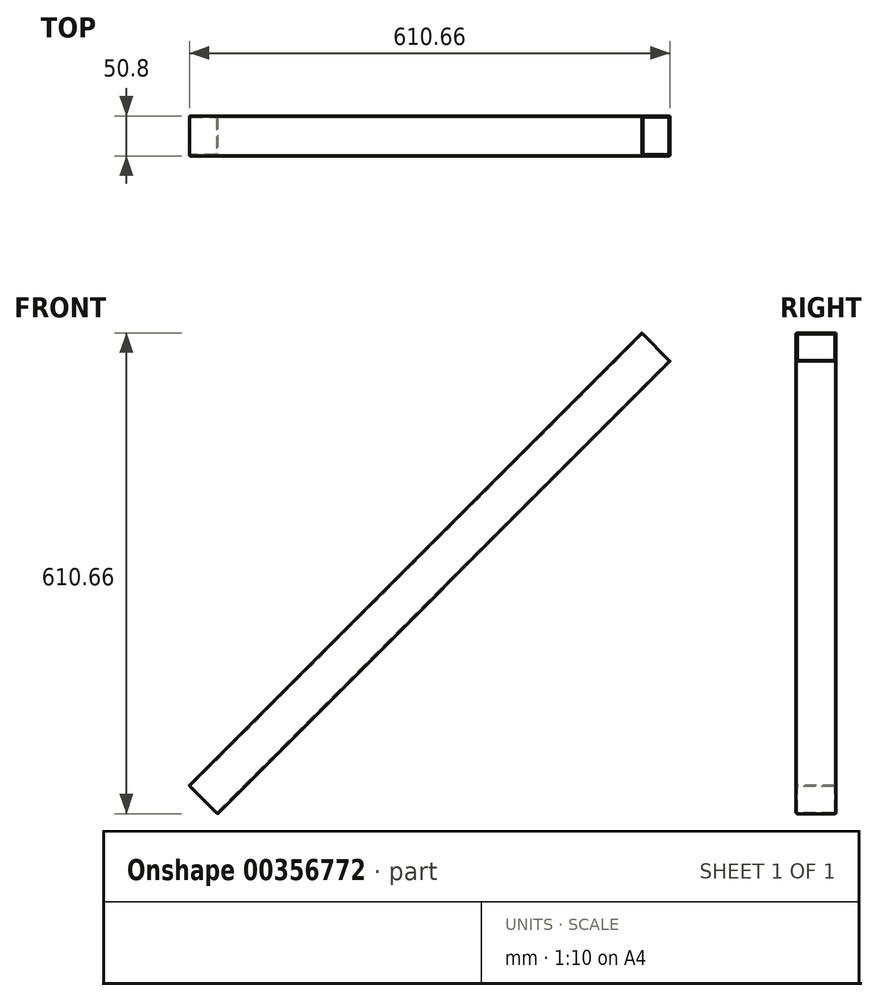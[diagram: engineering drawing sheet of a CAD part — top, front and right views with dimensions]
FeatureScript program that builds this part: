
annotation { "Feature Type Name" : "Feature", "Feature Type Description" : "" }
export const myFeature = defineFeature(function(context is Context, id is Id, definition is map)
    precondition{}
    {
        {
            var Q0;
            Q0=qCreatedBy(makeId("Front.planeOp"),FACE);
            var sketch = newSketch(context, id + "F0", { "sketchPlane" : qUnion([Q0])});
            skLineSegment(sketch, "E0.bottom", {"start": v(762, -381) * mm, "end": v(-762, -381) * mm});
            skLineSegment(sketch, "E0.top", {"start": v(762, 381) * mm, "end": v(-762, 381) * mm});
            skLineSegment(sketch, "E0.left", {"start": v(762, -381) * mm, "end": v(762, 381) * mm});
            skLineSegment(sketch, "E0.right", {"start": v(-762, -381) * mm, "end": v(-762, 381) * mm});
            skPoint(sketch, "E0.middle", {"position": v(0, 0) * mm});
            skLineSegment(sketch, "E1.bottom", {"start": v(-711.2, 330.2) * mm, "end": v(711.2, 330.2) * mm});
            skLineSegment(sketch, "E1.top", {"start": v(-711.2, -330.2) * mm, "end": v(711.2, -330.2) * mm});
            skLineSegment(sketch, "E1.left", {"start": v(-711.2, 330.2) * mm, "end": v(-711.2, -330.2) * mm});
            skLineSegment(sketch, "E1.right", {"start": v(711.2, 330.2) * mm, "end": v(711.2, -330.2) * mm});
            skSolve(sketch);
        }
        {
            var Q0;
            Q0=makeQuery(id+"F0.imprint","IMPRINT",FACE,{"disambiguationData":[TD([[makeQuery(id+"F0.imprint","IMPRINT",EDGE,{"derivedFrom":sQuery(id+"F0.wireOp",EDGE,"E1.bottom")}),-1.0]])]});
            var sketch = newSketch(context, id + "F1", { "sketchPlane" : qUnion([Q0])});
            skLineSegment(sketch, "E2", {"start": v(-711.2, -203.2) * mm, "end": v(-177.8, 330.2) * mm});
            skSolve(sketch);
        }
        {
            var Q0;
            Q0=sQuery(id+"F1.wireOp",EDGE,"E2");
            var Q1;
            Q1=sQuery(id+"F1.wireOp",VERTEX,"E2.start");
            cPlane(context, id + "F2", {"entities" : qUnion([Q0, Q1]), "cplaneType" : CPlaneType.CURVE_POINT, "offset" : 25.4 * mm, "width" : 152.4 * mm, "height" : 152.4 * mm});
        }
        {
            var Q0;
            Q0=qCreatedBy(id+"F2.planeOp",FACE);
            var sketch = newSketch(context, id + "F3", { "sketchPlane" : qUnion([Q0])});
            skLineSegment(sketch, "E3.bottom", {"start": v(-333.81, -25.4) * mm, "end": v(-384.61, -25.4) * mm});
            skLineSegment(sketch, "E3.top", {"start": v(-333.81, 25.4) * mm, "end": v(-384.61, 25.4) * mm});
            skLineSegment(sketch, "E3.left", {"start": v(-333.81, -25.4) * mm, "end": v(-333.81, 25.4) * mm});
            skLineSegment(sketch, "E3.right", {"start": v(-384.61, -25.4) * mm, "end": v(-384.61, 25.4) * mm});
            skPoint(sketch, "E3.middle", {"position": v(-359.21, 0) * mm});
            skLineSegment(sketch, "E4.bottom", {"start": v(-335.46, -23.75) * mm, "end": v(-382.96, -23.75) * mm});
            skLineSegment(sketch, "E4.top", {"start": v(-335.46, 23.75) * mm, "end": v(-382.96, 23.75) * mm});
            skLineSegment(sketch, "E4.left", {"start": v(-335.46, -23.75) * mm, "end": v(-335.46, 23.75) * mm});
            skLineSegment(sketch, "E4.right", {"start": v(-382.96, -23.75) * mm, "end": v(-382.96, 23.75) * mm});
            skSolve(sketch);
        }
        {
            var Q0;
            Q0=makeQuery(id+"F3.imprint","IMPRINT",FACE,{"disambiguationData":[TD([[makeQuery(id+"F3.imprint","IMPRINT",EDGE,{"derivedFrom":sQuery(id+"F3.wireOp",EDGE,"E3.bottom")}),-1.0]])]});
            extrude(context, id + "F4", {"entities" : qUnion([Q0]), "oppositeDirection" : true, "depth" : 25.4 * mm, "hasSecondDirection" : true, "secondDirectionOppositeDirection" : false, "secondDirectionDepth" : 787.4 * mm});
        }
        {
            var Q0;
            Q0=makeQuery(id+"F0.imprint","IMPRINT",FACE,{"disambiguationData":[TD([[makeQuery(id+"F0.imprint","IMPRINT",EDGE,{"derivedFrom":sQuery(id+"F0.wireOp",EDGE,"E0.bottom")}),-1.0]])]});
            extrude(context, id + "F5", {"entities" : qUnion([Q0]), "operationType" : NewBodyOperationType.REMOVE, "endBound" : BoundingType.SYMMETRIC, "oppositeDirection" : true, "depth" : 127 * mm});
        }
        {
            var Q0;
            Q0=makeQuery(id+"F4.opExtrude","SWEPT_EDGE",EDGE,{"disambiguationData":[OSD([sQuery(id+"F3.wireOp",EDGE,"E3.bottom"),sQuery(id+"F3.wireOp",EDGE,"E3.right")])]});
            var Q1;
            Q1=makeQuery(id+"F4.opExtrude","SWEPT_EDGE",EDGE,{"disambiguationData":[OSD([sQuery(id+"F3.wireOp",EDGE,"E3.top"),sQuery(id+"F3.wireOp",EDGE,"E3.right")])]});
            var Q2;
            Q2=makeQuery(id+"F4.opExtrude","SWEPT_EDGE",EDGE,{"disambiguationData":[OSD([sQuery(id+"F3.wireOp",EDGE,"E3.top"),sQuery(id+"F3.wireOp",EDGE,"E3.left")])]});
            var Q3;
            Q3=makeQuery(id+"F4.opExtrude","SWEPT_EDGE",EDGE,{"disambiguationData":[OSD([sQuery(id+"F3.wireOp",EDGE,"E3.bottom"),sQuery(id+"F3.wireOp",EDGE,"E3.left")])]});
            fillet(context, id + "F6", {"entities" : qUnion([Q0, Q1, Q2, Q3]), "radius" : 1.65 * mm, "tangentPropagation" : true, "allowEdgeOverflow" : false});
        }
        {
            var Q0;
            Q0=makeQuery(id+"F4.opExtrude","SWEPT_EDGE",EDGE,{"disambiguationData":[OSD([sQuery(id+"F3.wireOp",EDGE,"E4.top"),sQuery(id+"F3.wireOp",EDGE,"E4.left")])]});
            var Q1;
            Q1=makeQuery(id+"F4.opExtrude","SWEPT_EDGE",EDGE,{"disambiguationData":[OSD([sQuery(id+"F3.wireOp",EDGE,"E4.bottom"),sQuery(id+"F3.wireOp",EDGE,"E4.left")])]});
            var Q2;
            Q2=makeQuery(id+"F4.opExtrude","SWEPT_EDGE",EDGE,{"disambiguationData":[OSD([sQuery(id+"F3.wireOp",EDGE,"E4.bottom"),sQuery(id+"F3.wireOp",EDGE,"E4.right")])]});
            var Q3;
            Q3=makeQuery(id+"F4.opExtrude","SWEPT_EDGE",EDGE,{"disambiguationData":[OSD([sQuery(id+"F3.wireOp",EDGE,"E4.top"),sQuery(id+"F3.wireOp",EDGE,"E4.right")])]});
            fillet(context, id + "F7", {"entities" : qUnion([Q0, Q1, Q2, Q3]), "radius" : 1.65 * mm, "tangentPropagation" : true, "allowEdgeOverflow" : false});
        }
    });
